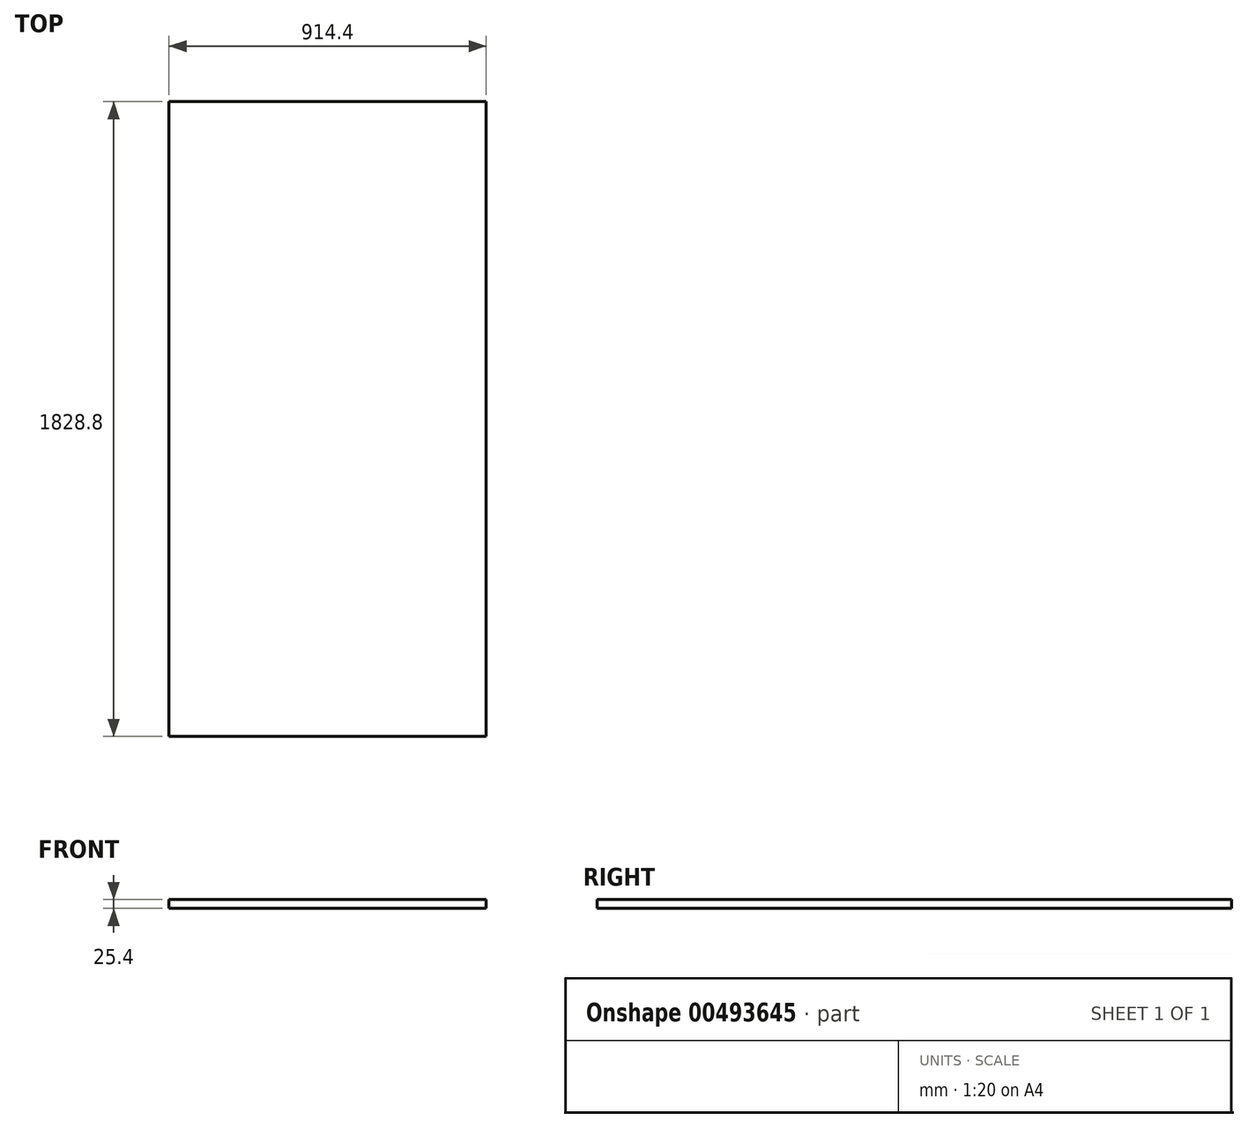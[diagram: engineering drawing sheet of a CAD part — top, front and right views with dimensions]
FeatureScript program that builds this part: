
annotation { "Feature Type Name" : "Feature", "Feature Type Description" : "" }
export const myFeature = defineFeature(function(context is Context, id is Id, definition is map)
    precondition{}
    {
        {
            var Q0;
            Q0=qCreatedBy(makeId("Top.planeOp"),FACE);
            var sketch = newSketch(context, id + "F0", { "sketchPlane" : qUnion([Q0])});
            skLineSegment(sketch, "E0.bottom", {"start": v(457.2, 914.4) * mm, "end": v(-457.2, 914.4) * mm});
            skLineSegment(sketch, "E0.top", {"start": v(457.2, -914.4) * mm, "end": v(-457.2, -914.4) * mm});
            skLineSegment(sketch, "E0.left", {"start": v(457.2, 914.4) * mm, "end": v(457.2, -914.4) * mm});
            skLineSegment(sketch, "E0.right", {"start": v(-457.2, 914.4) * mm, "end": v(-457.2, -914.4) * mm});
            skPoint(sketch, "E0.middle", {"position": v(0, 0) * mm});
            skSolve(sketch);
        }
        {
            var Q0;
            Q0=makeQuery(id+"F0.imprint","IMPRINT",FACE,{"disambiguationData":[TD([[makeQuery(id+"F0.imprint","IMPRINT",EDGE,{"derivedFrom":sQuery(id+"F0.wireOp",EDGE,"E0.bottom")}),1.0]])]});
            extrude(context, id + "F1", {"entities" : qUnion([Q0]), "depth" : 25.4 * mm});
        }
    });
